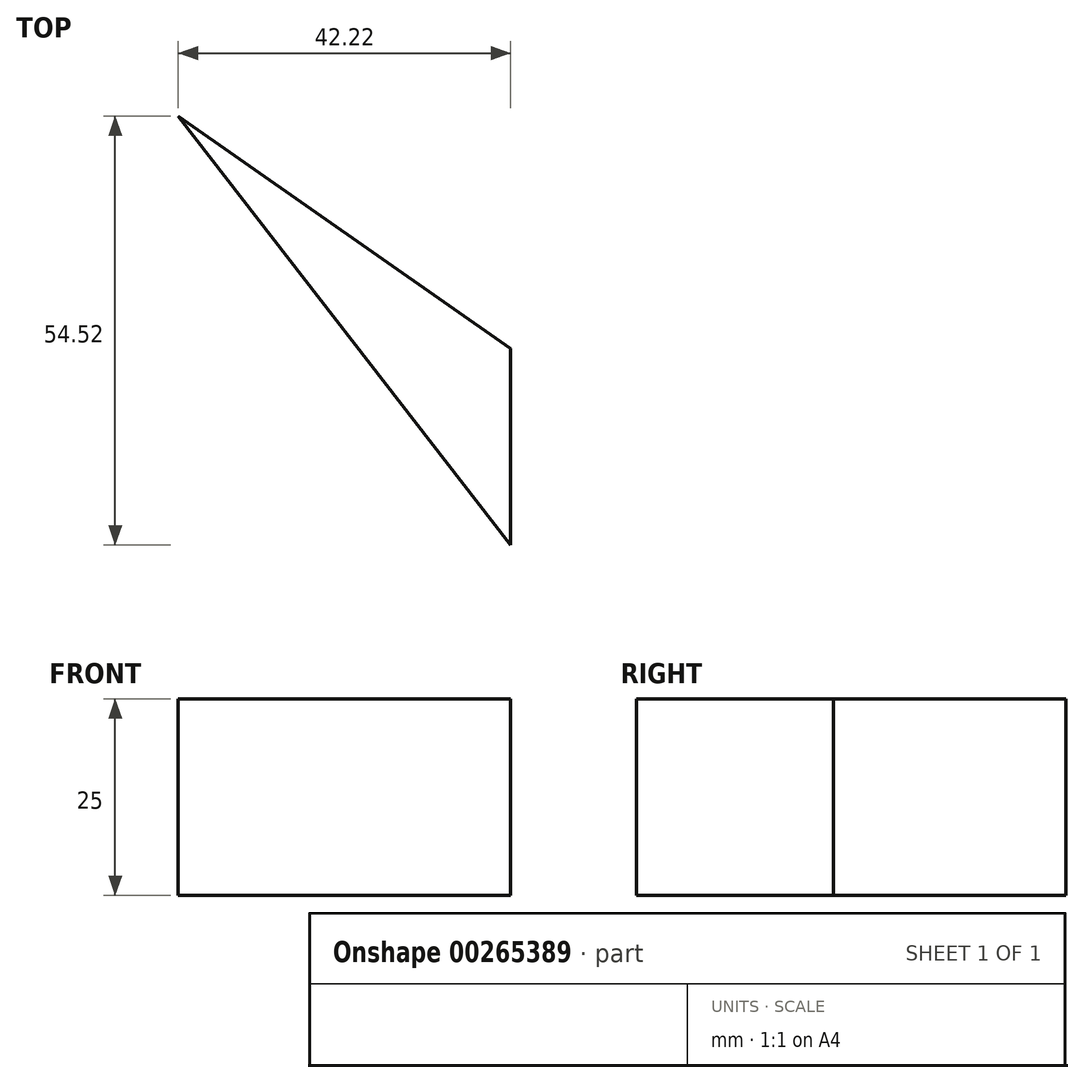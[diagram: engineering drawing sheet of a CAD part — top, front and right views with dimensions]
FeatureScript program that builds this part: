
annotation { "Feature Type Name" : "Feature", "Feature Type Description" : "" }
export const myFeature = defineFeature(function(context is Context, id is Id, definition is map)
    precondition{}
    {
        {
            var Q0;
            Q0=qCreatedBy(makeId("Top.planeOp"),FACE);
            var sketch = newSketch(context, id + "F0", { "sketchPlane" : qUnion([Q0])});
            skLineSegment(sketch, "E0", {"start": v(-61.68, 29.55) * mm, "end": v(22.76, 29.55) * mm});
            skLineSegment(sketch, "E1", {"start": v(-33.04, 29.55) * mm, "end": v(9.18, -24.97) * mm});
            skLineSegment(sketch, "E2", {"start": v(9.18, -24.97) * mm, "end": v(9.18, 0) * mm});
            skLineSegment(sketch, "E3", {"start": v(9.18, 0) * mm, "end": v(-33.04, 29.55) * mm});
            skLineSegment(sketch, "E4", {"start": v(-7.71, 11.82) * mm, "end": v(-7.71, -3.15) * mm});
            skSolve(sketch);
        }
        {
            var Q0;
            Q0 = qSketchRegion(id + "F0", true);
            extrude(context, id + "F1", {"entities" : qUnion([Q0]), "depth" : 25 * mm});
        }
    });
